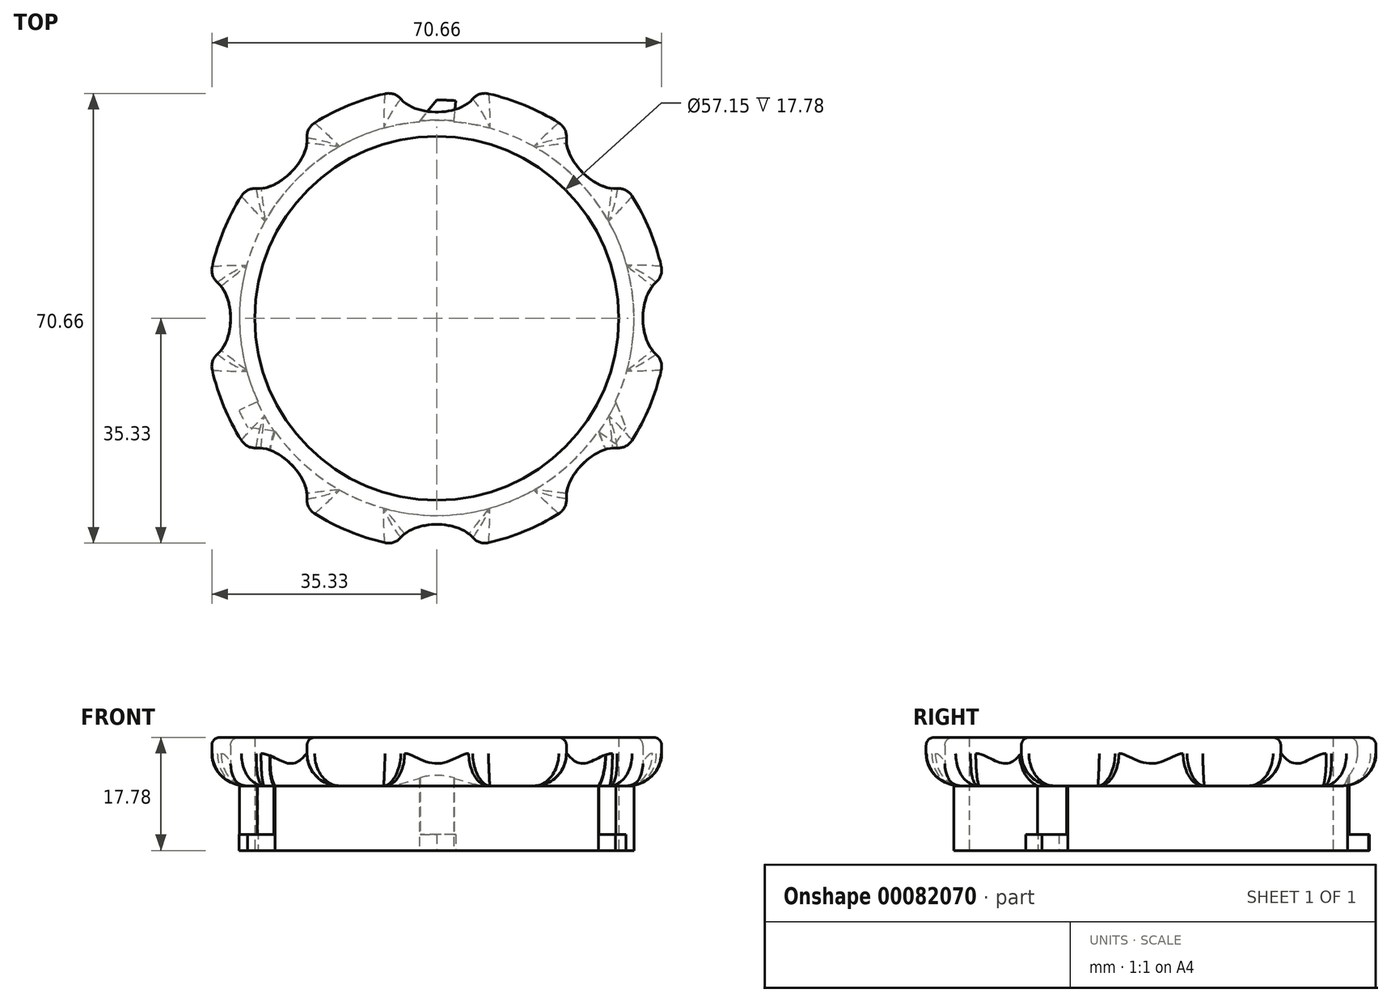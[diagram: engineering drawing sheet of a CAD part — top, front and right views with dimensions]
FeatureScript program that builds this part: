
annotation { "Feature Type Name" : "Feature", "Feature Type Description" : "" }
export const myFeature = defineFeature(function(context is Context, id is Id, definition is map)
    precondition{}
    {
        {
            var Q0;
            Q0=qCreatedBy(makeId("Top.planeOp"),FACE);
            var sketch = newSketch(context, id + "F0", { "sketchPlane" : qUnion([Q0])});
            skCircle(sketch, "E0", {"center": v(0, 0) * mm, "radius": 28.58 * mm});
            skArc(sketch, "E1", {"start": v(-2.7, 30.87) * mm, "mid": v(-26.84, 15.5) * mm, "end": v(-28.08, -13.1) * mm});
            skArc(sketch, "E2", {"start": v(-31.08, -14.5) * mm, "mid": v(-30.42, -15.83) * mm, "end": v(-29.7, -17.15) * mm});
            skLineSegment(sketch, "E3", {"start": v(0, 0) * mm, "end": v(0, 34.3) * mm, "construction": true});
            skLineSegment(sketch, "E4", {"start": v(0, 0) * mm, "end": v(29.7, -17.14) * mm, "construction": true});
            skLineSegment(sketch, "E5", {"start": v(0, 0) * mm, "end": v(-29.7, -17.15) * mm, "construction": true});
            skLineSegment(sketch, "E6", {"start": v(2.7, 30.87) * mm, "end": v(2.99, 34.16) * mm});
            skLineSegment(sketch, "E7", {"start": v(25.38, -17.77) * mm, "end": v(28.09, -19.67) * mm});
            skLineSegment(sketch, "E8", {"start": v(-28.08, -13.1) * mm, "end": v(-31.08, -14.5) * mm});
            skArc(sketch, "E9.trimOffspring", {"start": v(28.09, -19.67) * mm, "mid": v(28.92, -18.42) * mm, "end": v(29.7, -17.14) * mm});
            skArc(sketch, "E10.trimOffspring", {"start": v(2.99, 34.16) * mm, "mid": v(1.5, 34.26) * mm, "end": v(0, 34.3) * mm});
            skArc(sketch, "E11.trimOffspring", {"start": v(-25.38, -17.77) * mm, "mid": v(26.84, -15.5) * mm, "end": v(2.7, 30.87) * mm});
            skLineSegment(sketch, "E12", {"start": v(-2.7, 30.87) * mm, "end": v(0, 34.3) * mm});
            skLineSegment(sketch, "E13", {"start": v(28.08, -13.1) * mm, "end": v(29.7, -17.14) * mm});
            skLineSegment(sketch, "E14", {"start": v(-25.38, -17.77) * mm, "end": v(-29.7, -17.15) * mm});
            skSolve(sketch);
        }
        {
            var Q0;
            Q0 = qSketchRegion(id + "F0", true);
            extrude(context, id + "F1", {"entities" : qUnion([Q0]), "depth" : 2.54 * mm});
        }
        {
            var Q0;
            Q0=makeQuery(id+"F1.opExtrude","CAP_FACE",FACE,{"disambiguationData":[OSD([sQuery(id+"F0.wireOp",EDGE,"E0"),sQuery(id+"F0.wireOp",EDGE,"E1"),sQuery(id+"F0.wireOp",EDGE,"E2"),sQuery(id+"F0.wireOp",EDGE,"E6"),sQuery(id+"F0.wireOp",EDGE,"E7"),sQuery(id+"F0.wireOp",EDGE,"E8"),sQuery(id+"F0.wireOp",EDGE,"E9.trimOffspring"),sQuery(id+"F0.wireOp",EDGE,"E10.trimOffspring"),sQuery(id+"F0.wireOp",EDGE,"E11.trimOffspring"),sQuery(id+"F0.wireOp",EDGE,"E12"),sQuery(id+"F0.wireOp",EDGE,"E13"),sQuery(id+"F0.wireOp",EDGE,"E14")])],"isStart":false});
            var sketch = newSketch(context, id + "F2", { "sketchPlane" : qUnion([Q0])});
            skLineSegment(sketch, "E15.0.0", {"start": v(29.7, -17.14) * mm, "end": v(28.08, -13.1) * mm});
            skArc(sketch, "E15.0.1", {"start": v(28.08, -13.1) * mm, "mid": v(26.84, 15.5) * mm, "end": v(2.7, 30.87) * mm});
            skLineSegment(sketch, "E15.0.2", {"start": v(2.7, 30.87) * mm, "end": v(2.99, 34.16) * mm});
            skArc(sketch, "E15.0.3", {"start": v(2.99, 34.16) * mm, "mid": v(1.5, 34.26) * mm, "end": v(0, 34.3) * mm});
            skLineSegment(sketch, "E15.0.4", {"start": v(0, 34.3) * mm, "end": v(-2.7, 30.87) * mm});
            skArc(sketch, "E15.0.5", {"start": v(-2.7, 30.87) * mm, "mid": v(-26.84, 15.5) * mm, "end": v(-28.08, -13.1) * mm});
            skLineSegment(sketch, "E15.0.6", {"start": v(-28.08, -13.1) * mm, "end": v(-31.08, -14.5) * mm});
            skArc(sketch, "E15.0.7", {"start": v(-31.08, -14.5) * mm, "mid": v(-30.42, -15.83) * mm, "end": v(-29.7, -17.15) * mm});
            skLineSegment(sketch, "E15.0.8", {"start": v(-29.7, -17.15) * mm, "end": v(-25.38, -17.77) * mm});
            skArc(sketch, "E15.0.9", {"start": v(-25.38, -17.77) * mm, "mid": v(0, -30.99) * mm, "end": v(25.38, -17.77) * mm});
            skLineSegment(sketch, "E15.0.10", {"start": v(25.38, -17.77) * mm, "end": v(28.09, -19.67) * mm});
            skArc(sketch, "E15.0.11", {"start": v(28.09, -19.67) * mm, "mid": v(28.92, -18.42) * mm, "end": v(29.7, -17.14) * mm});
            skCircle(sketch, "E16", {"center": v(0, 0) * mm, "radius": 28.58 * mm});
            skCircle(sketch, "E17", {"center": v(0, 0) * mm, "radius": 31.12 * mm});
            skSolve(sketch);
        }
        {
            var Q0;
            Q0=makeQuery(id+"F2.imprint","IMPRINT",FACE,{"disambiguationData":[TD([[makeQuery(id+"F2.imprint","IMPRINT",EDGE,{"derivedFrom":sQuery(id+"F2.wireOp",EDGE,"E16")}),-1.0]])]});
            extrude(context, id + "F3", {"entities" : qUnion([Q0]), "operationType" : NewBodyOperationType.ADD, "depth" : 7.62 * mm});
        }
        {
            var Q0;
            Q0=makeQuery(id+"F3.opExtrude","CAP_FACE",FACE,{"disambiguationData":[OSD([sQuery(id+"F2.wireOp",EDGE,"E16"),sQuery(id+"F2.wireOp",EDGE,"E17")])],"isStart":false});
            var sketch = newSketch(context, id + "F4", { "sketchPlane" : qUnion([Q0])});
            skCircle(sketch, "E18", {"center": v(0, 0) * mm, "radius": 28.58 * mm});
            skArc(sketch, "E19", {"start": v(-8.14, 35.27) * mm, "mid": v(-13.85, 33.44) * mm, "end": v(-19.18, 30.7) * mm});
            skLineSegment(sketch, "E20", {"start": v(0, 0) * mm, "end": v(0, 36.2) * mm, "construction": true});
            skEllipticalArc(sketch, "E21", {});
            skPoint(sketch, "E22.visualSharp", {"position": v(-6.28, 35.65) * mm});
            skArc(sketch, "E22.filletArc", {"start": v(-5.64, 34.45) * mm, "mid": v(-6.78, 35.2) * mm, "end": v(-8.14, 35.27) * mm});
            skPoint(sketch, "E23.visualSharp", {"position": v(6.28, 35.65) * mm});
            skArc(sketch, "E23.filletArc", {"start": v(8.14, 35.27) * mm, "mid": v(6.78, 35.2) * mm, "end": v(5.64, 34.45) * mm});
            skEllipticalArc(sketch, "E24.1.0", {});
            skArc(sketch, "E24.1.1", {"start": v(-28.35, 20.37) * mm, "mid": v(-29.69, 20.1) * mm, "end": v(-30.7, 19.18) * mm});
            skArc(sketch, "E24.1.2", {"start": v(-19.18, 30.7) * mm, "mid": v(-20.1, 29.69) * mm, "end": v(-20.37, 28.35) * mm});
            skEllipticalArc(sketch, "E24.2.0", {});
            skArc(sketch, "E24.2.1", {"start": v(-34.45, -5.64) * mm, "mid": v(-35.2, -6.78) * mm, "end": v(-35.27, -8.14) * mm});
            skArc(sketch, "E24.2.2", {"start": v(-35.27, 8.14) * mm, "mid": v(-35.2, 6.78) * mm, "end": v(-34.45, 5.64) * mm});
            skEllipticalArc(sketch, "E24.3.0", {});
            skArc(sketch, "E24.3.1", {"start": v(-20.37, -28.35) * mm, "mid": v(-20.1, -29.69) * mm, "end": v(-19.18, -30.7) * mm});
            skArc(sketch, "E24.3.2", {"start": v(-30.7, -19.18) * mm, "mid": v(-29.69, -20.1) * mm, "end": v(-28.35, -20.37) * mm});
            skEllipticalArc(sketch, "E24.4.0", {});
            skArc(sketch, "E24.4.1", {"start": v(5.64, -34.45) * mm, "mid": v(6.78, -35.2) * mm, "end": v(8.14, -35.27) * mm});
            skArc(sketch, "E24.4.2", {"start": v(-8.14, -35.27) * mm, "mid": v(-6.78, -35.2) * mm, "end": v(-5.64, -34.45) * mm});
            skEllipticalArc(sketch, "E24.5.0", {});
            skArc(sketch, "E24.5.1", {"start": v(28.35, -20.37) * mm, "mid": v(29.69, -20.1) * mm, "end": v(30.7, -19.18) * mm});
            skArc(sketch, "E24.5.2", {"start": v(19.18, -30.7) * mm, "mid": v(20.1, -29.69) * mm, "end": v(20.37, -28.35) * mm});
            skEllipticalArc(sketch, "E24.6.0", {});
            skArc(sketch, "E24.6.1", {"start": v(34.45, 5.64) * mm, "mid": v(35.2, 6.78) * mm, "end": v(35.27, 8.14) * mm});
            skArc(sketch, "E24.6.2", {"start": v(35.27, -8.14) * mm, "mid": v(35.2, -6.78) * mm, "end": v(34.45, -5.64) * mm});
            skEllipticalArc(sketch, "E24.7.0", {});
            skArc(sketch, "E24.7.1", {"start": v(20.37, 28.35) * mm, "mid": v(20.1, 29.69) * mm, "end": v(19.18, 30.7) * mm});
            skArc(sketch, "E24.7.2", {"start": v(30.7, 19.18) * mm, "mid": v(29.69, 20.1) * mm, "end": v(28.35, 20.37) * mm});
            skArc(sketch, "E25.trimOffspring", {"start": v(-30.7, 19.18) * mm, "mid": v(-33.44, 13.85) * mm, "end": v(-35.27, 8.14) * mm});
            skArc(sketch, "E26.trimOffspring", {"start": v(-35.27, -8.14) * mm, "mid": v(-33.44, -13.85) * mm, "end": v(-30.7, -19.18) * mm});
            skArc(sketch, "E27.trimOffspring", {"start": v(-19.18, -30.7) * mm, "mid": v(-13.85, -33.44) * mm, "end": v(-8.14, -35.27) * mm});
            skArc(sketch, "E28.trimOffspring", {"start": v(8.14, -35.27) * mm, "mid": v(13.85, -33.44) * mm, "end": v(19.18, -30.7) * mm});
            skArc(sketch, "E29.trimOffspring", {"start": v(30.7, -19.18) * mm, "mid": v(33.44, -13.85) * mm, "end": v(35.27, -8.14) * mm});
            skArc(sketch, "E30.trimOffspring", {"start": v(35.27, 8.14) * mm, "mid": v(33.44, 13.85) * mm, "end": v(30.7, 19.18) * mm});
            skArc(sketch, "E31.trimOffspring", {"start": v(19.18, 30.7) * mm, "mid": v(13.85, 33.44) * mm, "end": v(8.14, 35.27) * mm});
            const initialGuessF4  = {"E21": [0, 0.036195, 1, 0, 0.00635, 0.00381, 3.6177938153336973, 5.806984145435682], "E24.1.0": [-0.02559372994504709, 0.025593729945047092, 0.7071067811865476, 0.7071067811865475, 0.00635, 0.00381, 3.6177938153336973, 5.806984145435682], "E24.2.0": [-0.036195, 0, 0, 1, 0.00635, 0.00381, 3.6177938153336973, 5.806984145435682], "E24.3.0": [-0.025593729945047092, -0.02559372994504709, -0.7071067811865475, 0.7071067811865476, 0.00635, 0.00381, 3.6177938153336973, 5.806984145435682], "E24.4.0": [0, -0.036195, -1, 0, 0.00635, 0.00381, 3.6177938153336973, 5.806984145435682], "E24.5.0": [0.02559372994504709, -0.025593729945047095, -0.7071067811865477, -0.7071067811865475, 0.00635, 0.00381, 3.6177938153336973, 5.806984145435682], "E24.6.0": [0.036195, 0, 0, -1, 0.00635, 0.00381, 3.6177938153336973, 5.806984145435682], "E24.7.0": [0.025593729945047095, 0.025593729945047085, 0.7071067811865474, -0.7071067811865477, 0.00635, 0.00381, 3.6177938153336973, 5.806984145435682]};
            skSetInitialGuess(sketch, initialGuessF4);
            skSolve(sketch);
        }
        {
            var Q0;
            Q0 = qSketchRegion(id + "F4", true);
            extrude(context, id + "F5", {"entities" : qUnion([Q0]), "operationType" : NewBodyOperationType.ADD, "depth" : 7.62 * mm});
        }
        {
            var Q0;
            Q0=makeQuery(id+"F5.opExtrude","CAP_EDGE",EDGE,{"disambiguationData":[OSD([sQuery(id+"F4.wireOp",EDGE,"E29.trimOffspring")])],"isStart":true});
            fillet(context, id + "F6", {"entities" : qUnion([Q0]), "radius" : 5.08 * mm, "tangentPropagation" : true, "allowEdgeOverflow" : false});
        }
        {
            var Q0;
            Q0=makeQuery(id+"F5.opExtrude","CAP_EDGE",EDGE,{"disambiguationData":[OSD([sQuery(id+"F4.wireOp",EDGE,"E30.trimOffspring")])],"isStart":false});
            fillet(context, id + "F7", {"entities" : qUnion([Q0]), "radius" : 1.27 * mm, "tangentPropagation" : true, "allowEdgeOverflow" : false});
        }
    });
